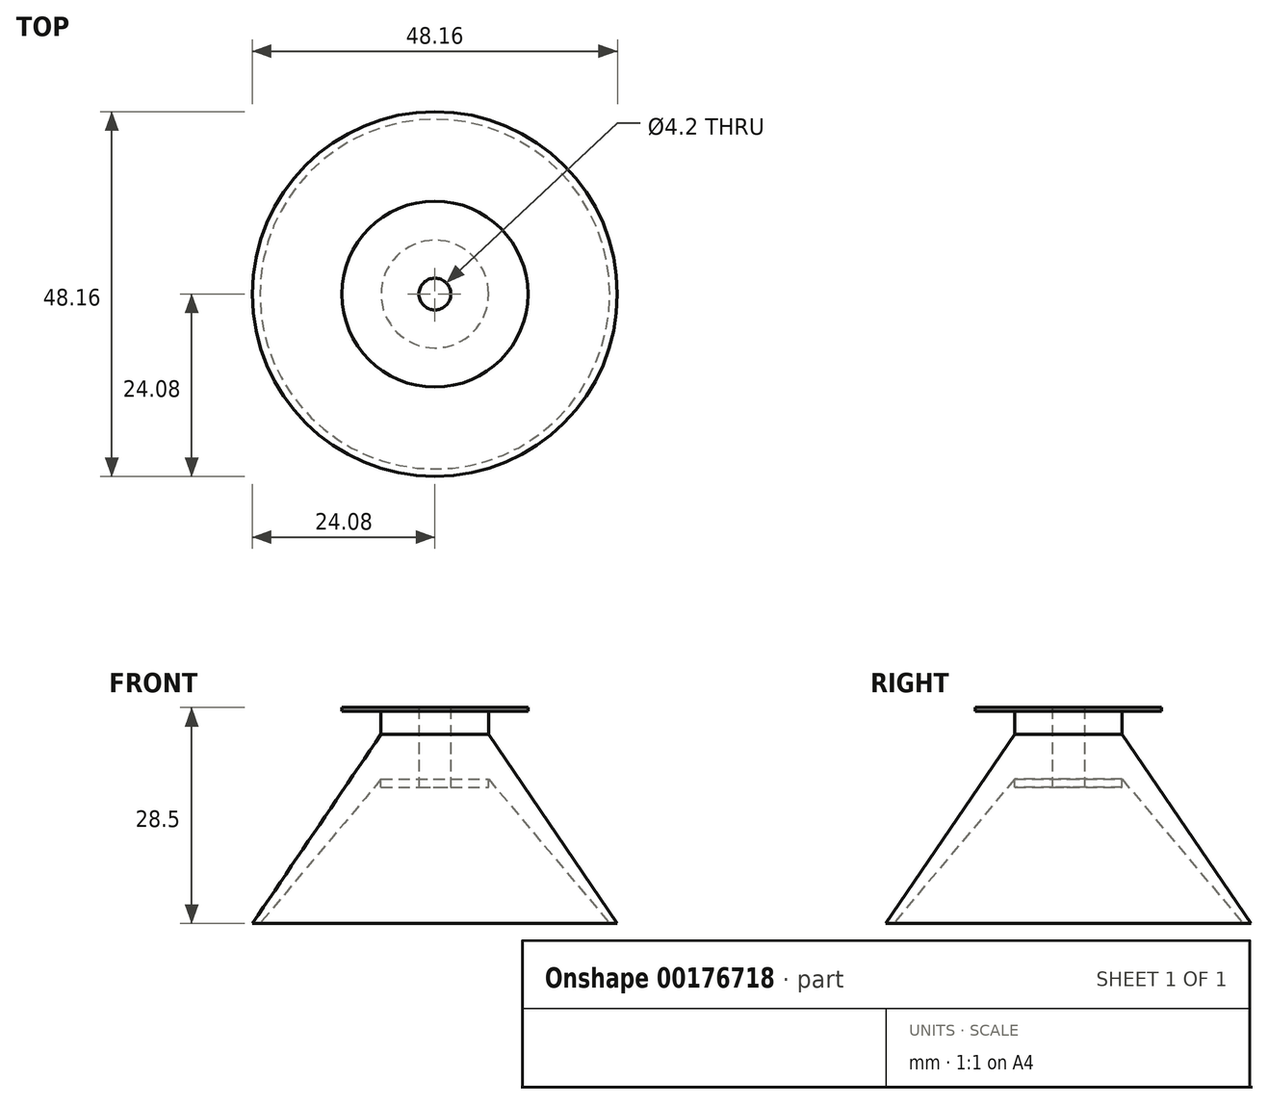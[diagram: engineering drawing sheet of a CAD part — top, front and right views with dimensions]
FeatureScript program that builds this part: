
annotation { "Feature Type Name" : "Feature", "Feature Type Description" : "" }
export const myFeature = defineFeature(function(context is Context, id is Id, definition is map)
    precondition{}
    {
        {
            var Q0;
            Q0=qCreatedBy(makeId("Front.planeOp"),FACE);
            var sketch = newSketch(context, id + "F0", { "sketchPlane" : qUnion([Q0])});
            skLineSegment(sketch, "E0", {"start": v(0, 0) * mm, "end": v(0, 25) * mm});
            skLineSegment(sketch, "E1", {"start": v(-2.1, 25) * mm, "end": v(-7.1, 25) * mm});
            skLineSegment(sketch, "E2", {"start": v(-7.1, 25) * mm, "end": v(-24.08, 0) * mm});
            skLineSegment(sketch, "E3", {"start": v(-24.08, 0) * mm, "end": v(-23.08, 0) * mm});
            skLineSegment(sketch, "E4", {"start": v(-23.08, 0) * mm, "end": v(-2.1, 25) * mm});
            skLineSegment(sketch, "E5", {"start": v(-7.1, 25) * mm, "end": v(-7.1, 28) * mm});
            skLineSegment(sketch, "E6", {"start": v(-7.1, 28) * mm, "end": v(-2.1, 28) * mm});
            skLineSegment(sketch, "E7", {"start": v(-2.1, 28) * mm, "end": v(-2.1, 25) * mm});
            skSolve(sketch);
        }
        {
            var Q0;
            Q0 = qSketchRegion(id + "F0", true);
            var Q1;
            Q1=sQuery(id+"F0.wireOp",EDGE,"E0");
            revolve(context, id + "F1", {"entities" : qUnion([Q0]), "axis" : qUnion([Q1]), "revolveType" : RevolveType.FULL});
        }
        {
            var Q0;
            Q0=makeQuery(id+"F1.opRevolve","SWEPT_FACE",FACE,{"disambiguationData":[OSD([sQuery(id+"F0.wireOp",EDGE,"E6")])]});
            extrude(context, id + "F2", {"entities" : qUnion([Q0]), "operationType" : NewBodyOperationType.ADD, "oppositeDirection" : true, "depth" : 10 * mm});
        }
        {
            var Q0;
            Q0=makeQuery(id+"F1.opRevolve","SWEPT_FACE",FACE,{"disambiguationData":[OSD([sQuery(id+"F0.wireOp",EDGE,"E6")])]});
            var sketch = newSketch(context, id + "F3", { "sketchPlane" : qUnion([Q0])});
            skCircle(sketch, "E8", {"center": v(0, 0) * mm, "radius": 12.28 * mm});
            skSolve(sketch);
        }
        {
            var Q0;
            Q0=makeQuery(id+"F3.imprint","IMPRINT",FACE,{"disambiguationData":[TD([[makeQuery(id+"F3.imprint","IMPRINT",EDGE,{"derivedFrom":sQuery(id+"F3.wireOp",EDGE,"E8")}),1.0]])]});
            var Q1;
            {var subQ0=sQuery(id+"F0.wireOp",EDGE,"E6");Q1=makeQuery(id+"F3.imprint","IMPRINT",FACE,{"disambiguationData":[TD([[makeQuery(id+"F3.imprint","IMPRINT",EDGE,{"derivedFrom":makeQuery(id+"F1.opRevolve","SWEPT_EDGE",EDGE,{"disambiguationData":[OSD([sQuery(id+"F0.wireOp",EDGE,"E5"),subQ0])]})}),-1.0]])]});}
            extrude(context, id + "F4", {"entities" : qUnion([Q0, Q1]), "operationType" : NewBodyOperationType.ADD, "depth" : 0.5 * mm});
        }
    });
